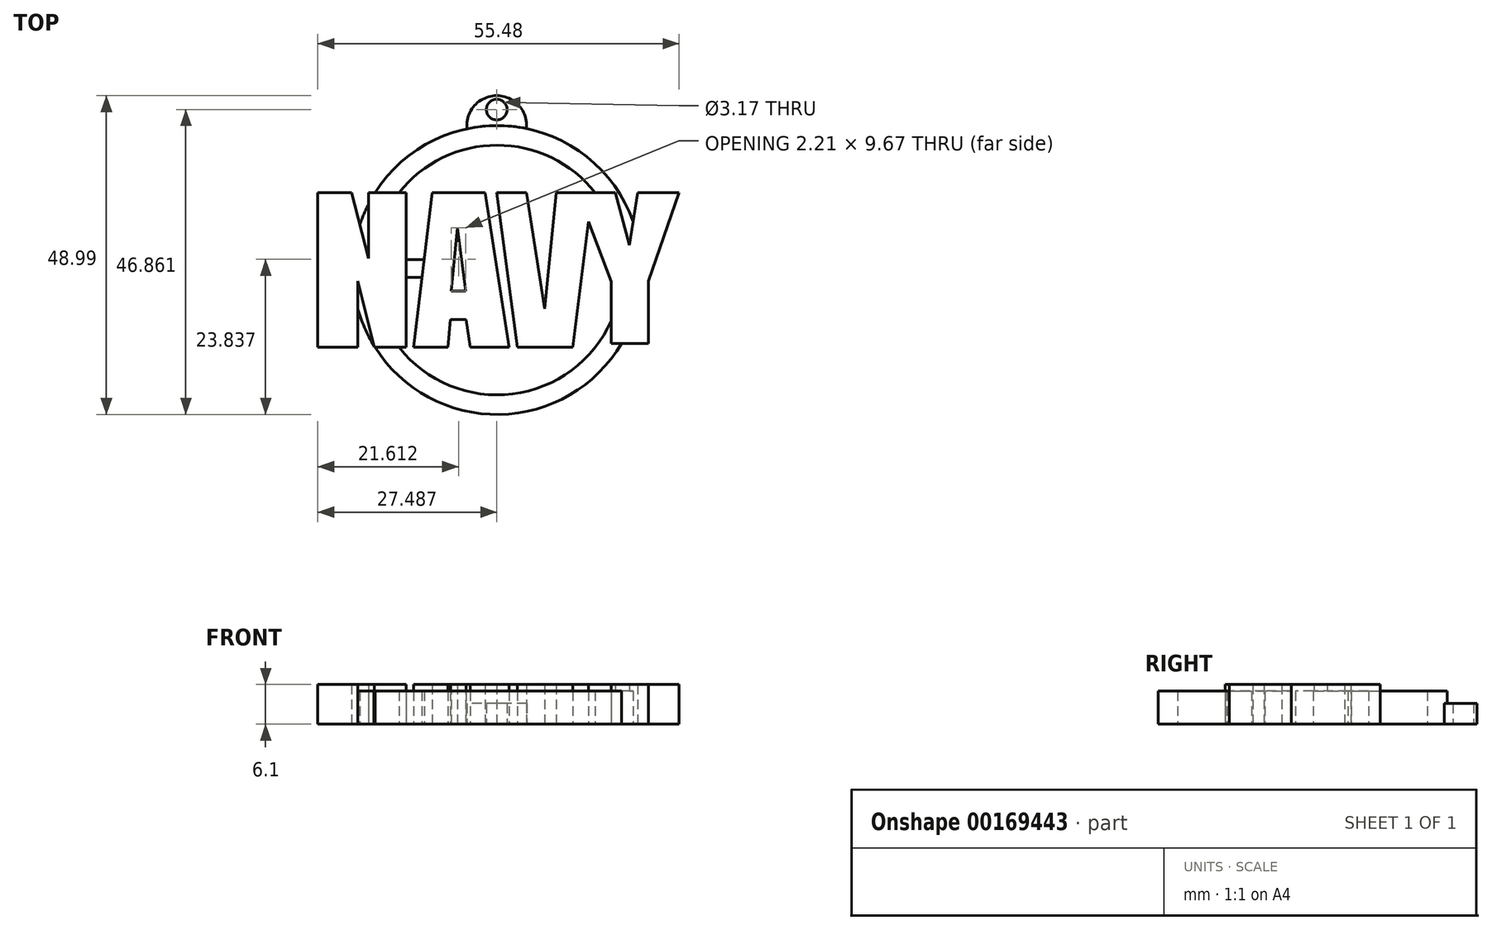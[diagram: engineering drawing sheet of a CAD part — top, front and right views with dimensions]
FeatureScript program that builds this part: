
annotation { "Feature Type Name" : "Feature", "Feature Type Description" : "" }
export const myFeature = defineFeature(function(context is Context, id is Id, definition is map)
    precondition{}
    {
        {
            var Q0;
            Q0=qCreatedBy(makeId("Top.planeOp"),FACE);
            var sketch = newSketch(context, id + "F0", { "sketchPlane" : qUnion([Q0])});
            skLineSegment(sketch, "E0", {"start": v(-29.4, 3.29) * mm, "end": v(-24.19, 3.29) * mm});
            skLineSegment(sketch, "E1", {"start": v(-24.19, 3.29) * mm, "end": v(-21.62, -6.82) * mm});
            skLineSegment(sketch, "E2", {"start": v(-21.62, -6.82) * mm, "end": v(-21.62, 3.29) * mm});
            skLineSegment(sketch, "E3", {"start": v(-21.62, 3.29) * mm, "end": v(-15.82, 3.29) * mm});
            skLineSegment(sketch, "E4", {"start": v(-15.82, 3.29) * mm, "end": v(-15.82, -20.49) * mm});
            skLineSegment(sketch, "E5", {"start": v(-15.82, -20.49) * mm, "end": v(-20.7, -20.49) * mm});
            skLineSegment(sketch, "E6", {"start": v(-20.7, -20.49) * mm, "end": v(-23.3, -10.32) * mm});
            skLineSegment(sketch, "E7", {"start": v(-23.3, -10.32) * mm, "end": v(-23.3, -20.49) * mm});
            skLineSegment(sketch, "E8", {"start": v(-29.4, 3.29) * mm, "end": v(-29.4, -20.49) * mm});
            skLineSegment(sketch, "E9", {"start": v(-29.4, -20.49) * mm, "end": v(-23.3, -20.49) * mm});
            skLineSegment(sketch, "E10", {"start": v(-14.7, -20.49) * mm, "end": v(-9.42, -20.49) * mm});
            skLineSegment(sketch, "E11", {"start": v(-9.42, -20.49) * mm, "end": v(-9.01, -16.23) * mm});
            skLineSegment(sketch, "E12", {"start": v(-9.01, -16.23) * mm, "end": v(-6.61, -16.23) * mm});
            skLineSegment(sketch, "E13", {"start": v(-6.61, -16.23) * mm, "end": v(-6.03, -20.49) * mm});
            skLineSegment(sketch, "E14", {"start": v(-6.03, -20.49) * mm, "end": v(0, -20.49) * mm});
            skLineSegment(sketch, "E15", {"start": v(0, -20.49) * mm, "end": v(-3.74, 3.29) * mm});
            skLineSegment(sketch, "E16", {"start": v(-3.74, 3.29) * mm, "end": v(-11.83, 3.29) * mm});
            skLineSegment(sketch, "E17", {"start": v(-11.83, 3.29) * mm, "end": v(-14.7, -20.49) * mm});
            skLineSegment(sketch, "E18", {"start": v(21.4, -10.3) * mm, "end": v(21.4, -19.86) * mm});
            skLineSegment(sketch, "E19", {"start": v(21.4, -19.86) * mm, "end": v(15.65, -19.86) * mm});
            skLineSegment(sketch, "E20", {"start": v(15.65, -19.86) * mm, "end": v(15.65, -10.37) * mm});
            skLineSegment(sketch, "E21", {"start": v(15.65, -10.37) * mm, "end": v(12.2, -1.17) * mm});
            skLineSegment(sketch, "E22", {"start": v(12.2, -1.17) * mm, "end": v(9.73, -20.49) * mm});
            skLineSegment(sketch, "E23", {"start": v(9.73, -20.49) * mm, "end": v(1.24, -20.49) * mm});
            skLineSegment(sketch, "E24", {"start": v(-7.94, -2.13) * mm, "end": v(-8.9, -11.8) * mm});
            skLineSegment(sketch, "E25", {"start": v(-8.9, -11.8) * mm, "end": v(-6.7, -11.8) * mm});
            skLineSegment(sketch, "E26", {"start": v(-6.7, -11.8) * mm, "end": v(-7.94, -2.13) * mm});
            skLineSegment(sketch, "E27", {"start": v(-1.92, 3.29) * mm, "end": v(2.65, 3.29) * mm});
            skLineSegment(sketch, "E28", {"start": v(-1.92, 3.29) * mm, "end": v(1.24, -20.49) * mm});
            skLineSegment(sketch, "E29", {"start": v(18.46, -4.8) * mm, "end": v(16.3, 3.29) * mm});
            skLineSegment(sketch, "E30", {"start": v(18.46, -4.8) * mm, "end": v(19.75, 3.29) * mm});
            skLineSegment(sketch, "E31", {"start": v(21.4, -10.3) * mm, "end": v(26.07, 3.29) * mm});
            skLineSegment(sketch, "E32", {"start": v(5.46, -14.53) * mm, "end": v(7.24, 3.29) * mm});
            skLineSegment(sketch, "E33", {"start": v(5.46, -14.53) * mm, "end": v(2.65, 3.29) * mm});
            skLineSegment(sketch, "E34.trimOffspring", {"start": v(7.24, 3.29) * mm, "end": v(16.3, 3.29) * mm});
            skLineSegment(sketch, "E35.trimOffspring", {"start": v(19.75, 3.29) * mm, "end": v(26.07, 3.29) * mm});
            skArc(sketch, "E36", {"start": v(-16.93, -20.49) * mm, "mid": v(0.5, -27.64) * mm, "end": v(15.65, -16.42) * mm});
            skArc(sketch, "E37", {"start": v(-21.62, 1.53) * mm, "mid": v(-22.34, -0.02) * mm, "end": v(-22.94, -1.62) * mm});
            skCircle(sketch, "E38", {"center": v(-1.92, 16.06) * mm, "radius": 1.59 * mm});
            skArc(sketch, "E39", {"start": v(2.65, 13.13) * mm, "mid": v(-1.93, 18.2) * mm, "end": v(-6.5, 13.1) * mm});
            skArc(sketch, "E40.trimOffspring", {"start": v(-23.3, -14.41) * mm, "mid": v(-22.24, -17.41) * mm, "end": v(-20.77, -20.23) * mm});
            skArc(sketch, "E41.trimOffspring", {"start": v(-20.61, -20.49) * mm, "mid": v(-1.5, -30.8) * mm, "end": v(17.26, -19.86) * mm});
            skArc(sketch, "E42.trimOffspring", {"start": v(13.19, 3.29) * mm, "mid": v(-1.87, 10.58) * mm, "end": v(-16.93, 3.29) * mm});
            skArc(sketch, "E43.trimOffspring", {"start": v(19.04, -1.16) * mm, "mid": v(0.6, 13.46) * mm, "end": v(-20.61, 3.29) * mm});
            skLineSegment(sketch, "E44", {"start": v(-15.82, -6.96) * mm, "end": v(-13.06, -6.96) * mm});
            skLineSegment(sketch, "E45", {"start": v(-0.56, -6.96) * mm, "end": v(-0.2, -9.72) * mm});
            skLineSegment(sketch, "E46", {"start": v(-0.2, -9.72) * mm, "end": v(-1.7, -9.72) * mm});
            skLineSegment(sketch, "E47.trimOffspring", {"start": v(-2.13, -6.96) * mm, "end": v(-0.56, -6.96) * mm});
            skLineSegment(sketch, "E48.trimOffspring", {"start": v(-13.4, -9.72) * mm, "end": v(-15.82, -9.72) * mm});
            skSolve(sketch);
        }
        {
            var Q0;
            {var subQ3=sQuery(id+"F0.wireOp",EDGE,"E0");Q0=makeQuery(id+"F0.imprint","IMPRINT",FACE,{"disambiguationData":[TD([[makeQuery(id+"F0.imprint","IMPRINT",EDGE,{"derivedFrom":subQ3}),-1.0]])]});}
            var Q1;
            Q1=makeQuery(id+"F0.imprint","IMPRINT",FACE,{"disambiguationData":[TD([[makeQuery(id+"F0.imprint","IMPRINT",EDGE,{"derivedFrom":sQuery(id+"F0.wireOp",EDGE,"E10")}),1.0]])]});
            var Q2;
            {var subQ6=sQuery(id+"F0.wireOp",EDGE,"E18");Q2=makeQuery(id+"F0.imprint","IMPRINT",FACE,{"disambiguationData":[TD([[makeQuery(id+"F0.imprint","IMPRINT",EDGE,{"derivedFrom":subQ6}),-1.0]])]});}
            var Q3;
            {var subQ0=sQuery(id+"F0.wireOp",EDGE,"HYzOr3BS-GEsO-tpgG-mHmg-E11RxQFouDff");var subQ1=sQuery(id+"F0.wireOp",EDGE,"E15");var subQ2=makeQuery(id+"F0.imprint","INTERSECT",VERTEX,{"disambiguationData":[OD(0.0)],"derivedFrom":[subQ1,subQ0]});Q3=makeQuery(id+"F0.imprint","IMPRINT",FACE,{"disambiguationData":[TD([[makeQuery(id+"F0.imprint","IMPRINT",EDGE,{"disambiguationData":[TD([[subQ2,-1.0]])],"derivedFrom":subQ1}),1.0]])]});}
            var Q4;
            {var subQ0=sQuery(id+"F0.wireOp",EDGE,"0SRW10ls-D7L2-GoXo-sYjI-dxRJMvZfKrfS");var subQ1=sQuery(id+"F0.wireOp",EDGE,"E15");var subQ2=makeQuery(id+"F0.imprint","INTERSECT",VERTEX,{"disambiguationData":[OD(0.0)],"derivedFrom":[subQ1,subQ0]});Q4=makeQuery(id+"F0.imprint","IMPRINT",FACE,{"disambiguationData":[TD([[makeQuery(id+"F0.imprint","IMPRINT",EDGE,{"disambiguationData":[TD([[subQ2,-1.0]])],"derivedFrom":subQ1}),1.0]])]});}
            var Q5;
            {var subQ0=sQuery(id+"F0.wireOp",EDGE,"0SRW10ls-D7L2-GoXo-sYjI-dxRJMvZfKrfS");var subQ1=sQuery(id+"F0.wireOp",EDGE,"E28");var subQ2=makeQuery(id+"F0.imprint","INTERSECT",VERTEX,{"disambiguationData":[OD(0.0)],"derivedFrom":[subQ1,subQ0]});Q5=makeQuery(id+"F0.imprint","IMPRINT",FACE,{"disambiguationData":[TD([[makeQuery(id+"F0.imprint","IMPRINT",EDGE,{"disambiguationData":[TD([[subQ2,-1.0]])],"derivedFrom":subQ1}),1.0]])]});}
            var Q6;
            {var subQ0=sQuery(id+"F0.wireOp",EDGE,"HYzOr3BS-GEsO-tpgG-mHmg-E11RxQFouDff");var subQ1=sQuery(id+"F0.wireOp",EDGE,"E28");var subQ2=makeQuery(id+"F0.imprint","INTERSECT",VERTEX,{"disambiguationData":[OD(0.0)],"derivedFrom":[subQ1,subQ0]});Q6=makeQuery(id+"F0.imprint","IMPRINT",FACE,{"disambiguationData":[TD([[makeQuery(id+"F0.imprint","IMPRINT",EDGE,{"disambiguationData":[TD([[subQ2,-1.0]])],"derivedFrom":subQ1}),1.0]])]});}
            extrude(context, id + "F1", {"entities" : qUnion([Q0, Q1, Q2, Q3, Q4, Q5, Q6]), "depth" : 6.1 * mm});
        }
        {
            var Q0;
            {var subQ1=sQuery(id+"F0.wireOp",EDGE,"E29");Q0=makeQuery(id+"F0.imprint","IMPRINT",FACE,{"disambiguationData":[TD([[makeQuery(id+"F0.imprint","IMPRINT",EDGE,{"derivedFrom":subQ1}),-1.0]])]});}
            var Q1;
            {var subQ3=sQuery(id+"F0.wireOp",EDGE,"E37");Q1=makeQuery(id+"F0.imprint","IMPRINT",FACE,{"disambiguationData":[TD([[makeQuery(id+"F0.imprint","IMPRINT",EDGE,{"derivedFrom":subQ3}),1.0]])]});}
            var Q2;
            {var subQ3=sQuery(id+"F0.wireOp",EDGE,"E40.trimOffspring");Q2=makeQuery(id+"F0.imprint","IMPRINT",FACE,{"disambiguationData":[TD([[makeQuery(id+"F0.imprint","IMPRINT",EDGE,{"derivedFrom":subQ3}),1.0]])]});}
            var Q3;
            {var subQ0=sQuery(id+"F0.wireOp",EDGE,"E36");Q3=makeQuery(id+"F0.imprint","IMPRINT",FACE,{"disambiguationData":[TD([[makeQuery(id+"F0.imprint","IMPRINT",EDGE,{"derivedFrom":subQ0}),-1.0]])]});}
            extrude(context, id + "F2", {"entities" : qUnion([Q0, Q1, Q2, Q3]), "operationType" : NewBodyOperationType.ADD, "depth" : 5.08 * mm});
        }
        {
            var Q0;
            Q0=makeQuery(id+"F0.imprint","IMPRINT",FACE,{"disambiguationData":[TD([[makeQuery(id+"F0.imprint","IMPRINT",EDGE,{"derivedFrom":sQuery(id+"F0.wireOp",EDGE,"E38")}),-1.0]])]});
            extrude(context, id + "F3", {"entities" : qUnion([Q0]), "operationType" : NewBodyOperationType.ADD, "depth" : 3.17 * mm});
        }
        {
            var Q0;
            {var subQ0=sQuery(id+"F0.wireOp",EDGE,"E44");Q0=makeQuery(id+"F0.imprint","IMPRINT",FACE,{"disambiguationData":[TD([[makeQuery(id+"F0.imprint","IMPRINT",EDGE,{"derivedFrom":subQ0}),-1.0]])]});}
            var Q1;
            Q1=makeQuery(id+"F0.imprint","IMPRINT",FACE,{"disambiguationData":[TD([[makeQuery(id+"F0.imprint","IMPRINT",EDGE,{"derivedFrom":sQuery(id+"F0.wireOp",EDGE,"E45")}),-1.0]])]});
            extrude(context, id + "F4", {"entities" : qUnion([Q0, Q1]), "operationType" : NewBodyOperationType.ADD, "depth" : 5.08 * mm});
        }
    });
